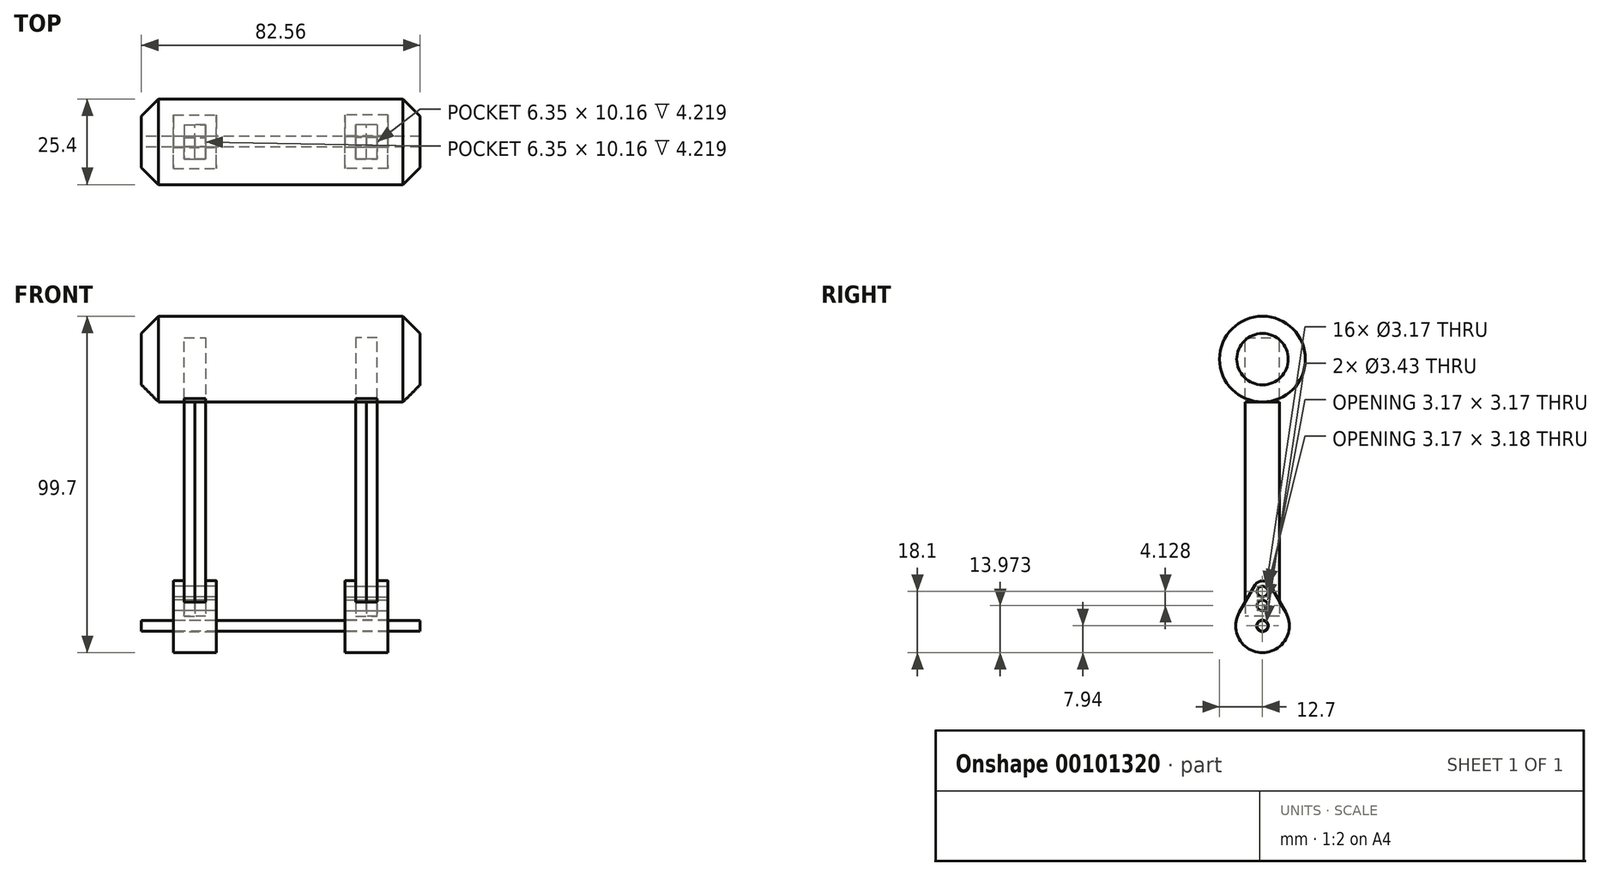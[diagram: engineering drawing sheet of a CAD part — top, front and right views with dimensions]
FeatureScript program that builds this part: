
annotation { "Feature Type Name" : "Feature", "Feature Type Description" : "" }
export const myFeature = defineFeature(function(context is Context, id is Id, definition is map)
    precondition{}
    {
        {
            var Q0;
            Q0=qCreatedBy(makeId("Right.planeOp"),FACE);
            var sketch = newSketch(context, id + "F0", { "sketchPlane" : qUnion([Q0])});
            skCircle(sketch, "E0", {"center": v(0, 0) * mm, "radius": 1.59 * mm});
            skSolve(sketch);
        }
        {
            var Q0;
            Q0 = qSketchRegion(id + "F0", true);
            extrude(context, id + "F1", {"entities" : qUnion([Q0]), "depth" : 41.27 * mm, "hasSecondDirection" : true, "secondDirectionOppositeDirection" : true, "secondDirectionDepth" : 41.27 * mm});
        }
        {
            var Q0;
            Q0=qCreatedBy(makeId("Right.planeOp"),FACE);
            cPlane(context, id + "F2", {"entities" : qUnion([Q0]), "cplaneType" : CPlaneType.OFFSET, "offset" : 25.4 * mm, "width" : 152.4 * mm, "height" : 152.4 * mm});
        }
        {
            var Q0;
            Q0=qCreatedBy(id+"F2.planeOp",FACE);
            var sketch = newSketch(context, id + "F3", { "sketchPlane" : qUnion([Q0])});
            skCircle(sketch, "E1", {"center": v(0, 0) * mm, "radius": 7.94 * mm});
            skCircle(sketch, "E2", {"center": v(0, 0) * mm, "radius": 1.71 * mm});
            skLineSegment(sketch, "E3", {"start": v(-6.87, 3.97) * mm, "end": v(-2.2, 12.07) * mm});
            skLineSegment(sketch, "E4", {"start": v(-6.87, 3.97) * mm, "end": v(0, 0) * mm, "construction": true});
            skLineSegment(sketch, "E5", {"start": v(-7.94, 0) * mm, "end": v(0, 0) * mm, "construction": true});
            skLineSegment(sketch, "E6", {"start": v(0, 0) * mm, "end": v(0, 15.88) * mm, "construction": true});
            skLineSegment(sketch, "E7.MirrorCS", {"start": v(6.87, 3.97) * mm, "end": v(2.2, 12.07) * mm});
            skPoint(sketch, "E8.visualSharp", {"position": v(0, 15.88) * mm});
            skArc(sketch, "E8.filletArc", {"start": v(2.2, 12.07) * mm, "mid": v(0, 13.34) * mm, "end": v(-2.2, 12.07) * mm});
            skSolve(sketch);
        }
        {
            var Q0;
            Q0 = qSketchRegion(id + "F3", true);
            extrude(context, id + "F4", {"entities" : qUnion([Q0]), "depth" : 6.35 * mm, "hasSecondDirection" : true, "secondDirectionOppositeDirection" : true, "secondDirectionDepth" : 6.35 * mm});
        }
        {
            var Q0;
            Q0=qCreatedBy(makeId("Front.planeOp"),FACE);
            var sketch = newSketch(context, id + "F5", { "sketchPlane" : qUnion([Q0])});
            skLineSegment(sketch, "E9", {"start": v(22.23, 13.02) * mm, "end": v(22.23, 2.86) * mm});
            skLineSegment(sketch, "E10", {"start": v(22.23, 2.86) * mm, "end": v(28.58, 2.86) * mm});
            skLineSegment(sketch, "E11", {"start": v(28.57, 2.86) * mm, "end": v(28.57, 13.02) * mm});
            skLineSegment(sketch, "E12", {"start": v(31.75, -7.94) * mm, "end": v(19.05, -7.94) * mm});
            skLineSegment(sketch, "E13", {"start": v(25.4, -7.94) * mm, "end": v(12.7, -7.94) * mm});
            skLineSegment(sketch, "E14", {"start": v(31.75, 1.71) * mm, "end": v(31.75, 7.94) * mm, "construction": true});
            skLineSegment(sketch, "E15", {"start": v(31.75, -7.94) * mm, "end": v(31.75, -1.71) * mm, "construction": true});
            skLineSegment(sketch, "E16", {"start": v(19.05, 1.71) * mm, "end": v(19.05, 7.94) * mm, "construction": true});
            skLineSegment(sketch, "E17", {"start": v(19.05, -7.94) * mm, "end": v(19.05, -1.71) * mm, "construction": true});
            skLineSegment(sketch, "E18", {"start": v(19.05, 2.86) * mm, "end": v(22.23, 2.86) * mm, "construction": true});
            skLineSegment(sketch, "E19", {"start": v(28.58, 2.86) * mm, "end": v(31.75, 2.86) * mm, "construction": true});
            skLineSegment(sketch, "E20", {"start": v(28.57, 13.02) * mm, "end": v(22.23, 13.02) * mm});
            skSolve(sketch);
        }
        {
            var Q0;
            Q0 = qSketchRegion(id + "F5", true);
            extrude(context, id + "F6", {"entities" : qUnion([Q0]), "operationType" : NewBodyOperationType.REMOVE, "oppositeDirection" : true, "depth" : 5.08 * mm, "hasSecondDirection" : true, "secondDirectionOppositeDirection" : false, "secondDirectionDepth" : 5.08 * mm});
        }
        {
            var Q0;
            Q0=qCreatedBy(id+"F2.planeOp",FACE);
            var sketch = newSketch(context, id + "F7", { "sketchPlane" : qUnion([Q0])});
            skLineSegment(sketch, "E21.0.1", {"start": v(-5.08, 2.86) * mm, "end": v(5.08, 2.86) * mm});
            skLineSegment(sketch, "E21.0.3", {"start": v(5.08, 2.86) * mm, "end": v(-5.08, 2.86) * mm});
            skLineSegment(sketch, "E22.0.1", {"start": v(-5.08, 7.08) * mm, "end": v(-5.08, 2.86) * mm});
            skLineSegment(sketch, "E22.0.3", {"start": v(-5.08, 2.86) * mm, "end": v(-5.08, 7.08) * mm});
            skLineSegment(sketch, "E23.0.1", {"start": v(5.08, 7.08) * mm, "end": v(5.08, 2.86) * mm});
            skLineSegment(sketch, "E23.0.3", {"start": v(5.08, 2.86) * mm, "end": v(5.08, 7.08) * mm});
            skLineSegment(sketch, "E24", {"start": v(0, 2.86) * mm, "end": v(0, 79.06) * mm, "construction": true});
            skPoint(sketch, "E24.endSnap0", {"position": v(0, 2.86) * mm});
            skPoint(sketch, "E25.endSnap0", {"position": v(0, 40.96) * mm});
            skLineSegment(sketch, "E26", {"start": v(-5.08, 7.08) * mm, "end": v(-5.08, 79.06) * mm});
            skArc(sketch, "E27", {"start": v(-5.08, 79.06) * mm, "mid": v(-3.6, 82.65) * mm, "end": v(0, 84.14) * mm});
            skArc(sketch, "E28.MirrorCS", {"start": v(5.08, 79.06) * mm, "mid": v(3.6, 82.65) * mm, "end": v(0, 84.14) * mm});
            skLineSegment(sketch, "E29.MirrorCS", {"start": v(5.08, 7.08) * mm, "end": v(5.08, 79.06) * mm});
            skLineSegment(sketch, "E30", {"start": v(-5.08, 79.06) * mm, "end": v(5.08, 79.06) * mm, "construction": true});
            skSolve(sketch);
        }
        {
            var Q0;
            Q0 = qSketchRegion(id + "F7", true);
            extrude(context, id + "F8", {"entities" : qUnion([Q0]), "depth" : 3.17 * mm});
        }
        {
            var Q0;
            Q0 = qSketchRegion(id + "F7", true);
            extrude(context, id + "F9", {"entities" : qUnion([Q0]), "oppositeDirection" : true, "depth" : 3.17 * mm});
        }
        {
            var Q0;
            Q0=qCreatedBy(id+"F2.planeOp",FACE);
            var sketch = newSketch(context, id + "F10", { "sketchPlane" : qUnion([Q0])});
            skLineSegment(sketch, "E31", {"start": v(0, 2.86) * mm, "end": v(0, 13.34) * mm, "construction": true});
            skCircle(sketch, "E32", {"center": v(0, 6.03) * mm, "radius": 1.59 * mm});
            skCircle(sketch, "E33", {"center": v(0, 10.16) * mm, "radius": 1.59 * mm});
            skSolve(sketch);
        }
        {
            var Q0;
            Q0 = qSketchRegion(id + "F10", true);
            extrude(context, id + "F11", {"entities" : qUnion([Q0]), "operationType" : NewBodyOperationType.REMOVE, "oppositeDirection" : true, "depth" : 25.4 * mm, "hasSecondDirection" : true, "secondDirectionOppositeDirection" : false, "secondDirectionDepth" : 25.4 * mm});
        }
        {
            var Q0;
            Q0=makeQuery(id+"F9.opExtrude","SWEPT_BODY",BODY,{"disambiguationData":[OSD([sQuery(id+"F7.wireOp",EDGE,"E21.0.3"),sQuery(id+"F7.wireOp",EDGE,"E22.0.3"),sQuery(id+"F7.wireOp",EDGE,"E23.0.3"),sQuery(id+"F7.wireOp",EDGE,"E26"),sQuery(id+"F7.wireOp",EDGE,"E27"),sQuery(id+"F7.wireOp",EDGE,"E28.MirrorCS"),sQuery(id+"F7.wireOp",EDGE,"E29.MirrorCS")])]});
            var Q1;
            Q1=makeQuery(id+"F8.opExtrude","SWEPT_BODY",BODY,{"disambiguationData":[OSD([sQuery(id+"F7.wireOp",EDGE,"E21.0.3"),sQuery(id+"F7.wireOp",EDGE,"E22.0.3"),sQuery(id+"F7.wireOp",EDGE,"E23.0.3"),sQuery(id+"F7.wireOp",EDGE,"E26"),sQuery(id+"F7.wireOp",EDGE,"E27"),sQuery(id+"F7.wireOp",EDGE,"E28.MirrorCS"),sQuery(id+"F7.wireOp",EDGE,"E29.MirrorCS")])]});
            var Q2;
            Q2=makeQuery(id+"F4.opExtrude","SWEPT_BODY",BODY,{"disambiguationData":[OSD([sQuery(id+"F3.wireOp",EDGE,"E1"),sQuery(id+"F3.wireOp",EDGE,"E2"),sQuery(id+"F3.wireOp",EDGE,"E3"),sQuery(id+"F3.wireOp",EDGE,"E7.MirrorCS"),sQuery(id+"F3.wireOp",EDGE,"E8.filletArc")])]});
            var Q3;
            Q3=qCreatedBy(makeId("Right.planeOp"),FACE);
            mirror(context, id + "F12", {"entities" : qUnion([Q0, Q1, Q2]), "mirrorPlane" : qUnion([Q3])});
        }
        {
            var Q0;
            Q0=qCreatedBy(makeId("Right.planeOp"),FACE);
            var sketch = newSketch(context, id + "F13", { "sketchPlane" : qUnion([Q0])});
            skCircle(sketch, "E34", {"center": v(0, 79.06) * mm, "radius": 12.7 * mm});
            skSolve(sketch);
        }
        {
            var Q0;
            Q0=makeQuery(id+"F13.imprint","IMPRINT",FACE,{"disambiguationData":[TD([[makeQuery(id+"F13.imprint","IMPRINT",EDGE,{"derivedFrom":sQuery(id+"F13.wireOp",EDGE,"E34")}),1.0]])]});
            extrude(context, id + "F14", {"entities" : qUnion([Q0]), "depth" : 41.27 * mm, "hasSecondDirection" : true, "secondDirectionOppositeDirection" : true, "secondDirectionDepth" : 41.27 * mm});
        }
        {
            var Q0;
            Q0=makeQuery(id+"F14.opExtrude","CAP_EDGE",EDGE,{"disambiguationData":[OSD([sQuery(id+"F13.wireOp",EDGE,"E34")])],"isStart":false});
            var Q1;
            Q1=makeQuery(id+"F14.opExtrude","CAP_EDGE",EDGE,{"disambiguationData":[OSD([sQuery(id+"F13.wireOp",EDGE,"E34")])],"isStart":true});
            chamfer(context, id + "F15", {"entities" : qUnion([Q0, Q1]), "width" : 5.08 * mm, "tangentPropagation" : true});
        }
        {
            var Q0;
            Q0=qCreatedBy(makeId("Front.planeOp"),FACE);
            var sketch = newSketch(context, id + "F16", { "sketchPlane" : qUnion([Q0])});
            skLineSegment(sketch, "E35.0", {"start": v(-28.58, 2.86) * mm, "end": v(-28.58, 79.06) * mm, "construction": true});
            skLineSegment(sketch, "E36", {"start": v(-28.58, 66.36) * mm, "end": v(-28.58, 85.4) * mm});
            skLineSegment(sketch, "E37", {"start": v(-28.58, 85.4) * mm, "end": v(-22.23, 85.4) * mm});
            skLineSegment(sketch, "E38", {"start": v(-22.23, 85.4) * mm, "end": v(-22.23, 66.36) * mm});
            skLineSegment(sketch, "E39", {"start": v(-28.58, 66.36) * mm, "end": v(-22.23, 66.36) * mm});
            skLineSegment(sketch, "E40", {"start": v(0, 85.4) * mm, "end": v(0, 66.36) * mm, "construction": true});
            skLineSegment(sketch, "E41.0", {"start": v(-36.2, 91.76) * mm, "end": v(-36.2, 66.36) * mm, "construction": true});
            skLineSegment(sketch, "E42.MirrorCS", {"start": v(28.58, 85.4) * mm, "end": v(22.23, 85.4) * mm});
            skLineSegment(sketch, "E43.MirrorCS", {"start": v(28.58, 2.86) * mm, "end": v(28.58, 79.06) * mm, "construction": true});
            skLineSegment(sketch, "E44.MirrorCS", {"start": v(28.58, 66.36) * mm, "end": v(28.58, 85.4) * mm});
            skLineSegment(sketch, "E45.MirrorCS", {"start": v(22.23, 85.4) * mm, "end": v(22.23, 66.36) * mm});
            skLineSegment(sketch, "E46.MirrorCS", {"start": v(28.58, 66.36) * mm, "end": v(22.23, 66.36) * mm});
            skSolve(sketch);
        }
        {
            var Q0;
            Q0 = qSketchRegion(id + "F16", true);
            extrude(context, id + "F17", {"entities" : qUnion([Q0]), "operationType" : NewBodyOperationType.REMOVE, "depth" : 5.08 * mm, "hasSecondDirection" : true, "secondDirectionOppositeDirection" : true, "secondDirectionDepth" : 5.08 * mm});
        }
    });
